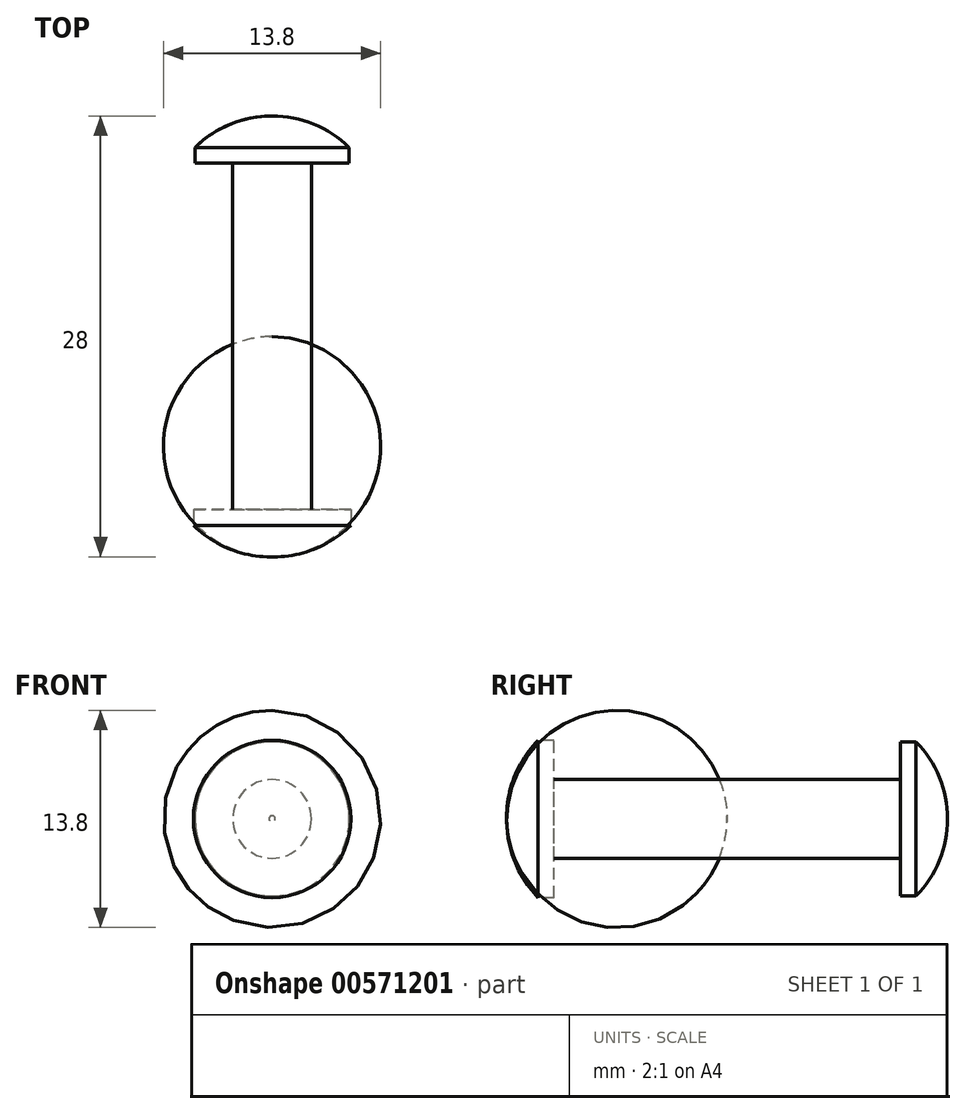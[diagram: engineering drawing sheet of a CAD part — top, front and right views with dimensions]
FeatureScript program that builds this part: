
annotation { "Feature Type Name" : "Feature", "Feature Type Description" : "" }
export const myFeature = defineFeature(function(context is Context, id is Id, definition is map)
    precondition{}
    {
        {
            var Q0;
            Q0=qCreatedBy(makeId("Top.planeOp"),FACE);
            var sketch = newSketch(context, id + "F0", { "sketchPlane" : qUnion([Q0])});
            skLineSegment(sketch, "E0", {"start": v(-2.5, 22) * mm, "end": v(-2.5, 0) * mm});
            skLineSegment(sketch, "E1", {"start": v(-2.5, 0) * mm, "end": v(-5, 0) * mm});
            skLineSegment(sketch, "E2", {"start": v(-5, 0) * mm, "end": v(-5, -1) * mm});
            skPoint(sketch, "E3.center.orphan", {"position": v(0, 11) * mm});
            skArc(sketch, "E4", {"start": v(-5, -1) * mm, "mid": v(-2.7, -2.5) * mm, "end": v(0, -3) * mm});
            skLineSegment(sketch, "E5", {"start": v(-2.5, 22) * mm, "end": v(-4.9, 22) * mm});
            skLineSegment(sketch, "E6", {"start": v(-4.9, 22) * mm, "end": v(-4.9, 23) * mm});
            skPoint(sketch, "E7", {"position": v(0, 10) * mm});
            skArc(sketch, "E8", {"start": v(0, 25) * mm, "mid": v(-2.65, 24.48) * mm, "end": v(-4.9, 23) * mm});
            skPoint(sketch, "E9.start.orphan", {"position": v(0, 22) * mm});
            skPoint(sketch, "E10.start.orphan", {"position": v(0, 0) * mm});
            skLineSegment(sketch, "E11", {"start": v(0, -3) * mm, "end": v(0, 25) * mm});
            skSolve(sketch);
        }
        {
            var Q0;
            Q0=makeQuery(id+"F0.imprint","IMPRINT",FACE,{"disambiguationData":[TD([[makeQuery(id+"F0.imprint","IMPRINT",EDGE,{"derivedFrom":sQuery(id+"F0.wireOp",EDGE,"E0")}),1.0]])]});
            var Q1;
            Q1=sQuery(id+"F0.wireOp",EDGE,"E11");
            revolve(context, id + "F1", {"entities" : qUnion([Q0]), "axis" : qUnion([Q1]), "revolveType" : RevolveType.FULL});
        }
    });
